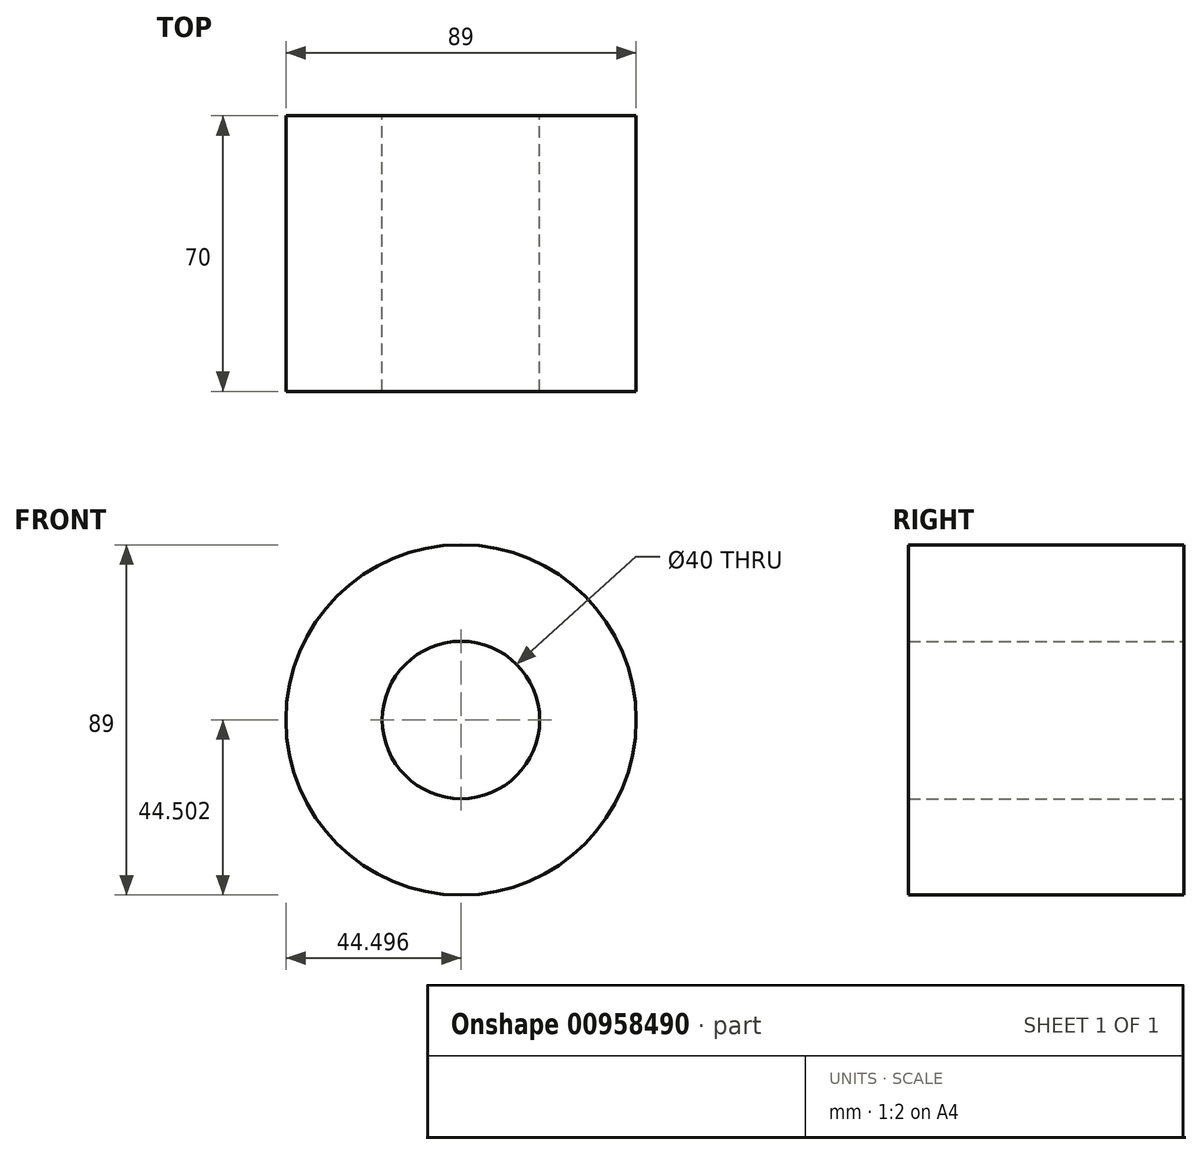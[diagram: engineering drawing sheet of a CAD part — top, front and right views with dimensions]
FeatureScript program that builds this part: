
annotation { "Feature Type Name" : "Feature", "Feature Type Description" : "" }
export const myFeature = defineFeature(function(context is Context, id is Id, definition is map)
    precondition{}
    {
        {
            var Q0;
            Q0=qCreatedBy(makeId("Front.planeOp"),FACE);
            var sketch = newSketch(context, id + "F0", { "sketchPlane" : qUnion([Q0])});
            skCircle(sketch, "E0", {"center": v(251.45, -96.2) * mm, "radius": 20 * mm});
            skCircle(sketch, "E1", {"center": v(251.45, -96.2) * mm, "radius": 44.5 * mm});
            skSolve(sketch);
        }
        {
            var Q0;
            Q0=makeQuery(id+"F0.imprint","IMPRINT",FACE,{"disambiguationData":[TD([[makeQuery(id+"F0.imprint","IMPRINT",EDGE,{"derivedFrom":sQuery(id+"F0.wireOp",EDGE,"E0")}),-1.0]])]});
            extrude(context, id + "F1", {"entities" : qUnion([Q0]), "depth" : 70 * mm, "offsetDistance" : 25 * mm});
        }
    });
